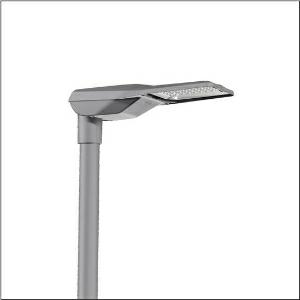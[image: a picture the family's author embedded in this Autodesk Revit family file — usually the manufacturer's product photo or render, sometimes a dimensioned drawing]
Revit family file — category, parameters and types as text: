
# Revit family: streetlight_sl_21_iq_mini___stw1_0a_5xe2e31g08jb_fb58
name_source: partatom
category: Lighting Fixtures
units: mm (PartAtom-declared; Revit-internal decimal feet)

## family parameters
Cut with Voids When Loaded = No
Host = Face
Light Source = No
Part Type = Normal
Room Calculation Point = No
Round Connector Dimension = Use Diameter
Shared = No

## types (1)
- --- (1 x LED, 10820 lm, 71.6 W, 3000K)
    Apparent Load = 72 VA
    CIE Flux Codes = 39 75 98 100 100
    Color Rendering = 70
    Color Temperature = 3000K
    Default Elevation = 1800 mm
    Description = Streetlight SL 21 iQ mini, mast luminaire, primary light control with lens, of PMMA, primary optical cover: cover, of toughened safety glass, transparent, light distribution: STW1.0a, light emission: direct distribution, primary light characteristic: asymmetric, installation type: post-top, side-entry, LED, High Power LED, rated luminous flux: 10.820lm, luminous efficacy: 151lm/W, light colour: 730, colour temperature: 3000K, control gear: iQ Street-Remote, control: Street-Remote, Auto-Match, Temp-Guard, Lumen-Switch, Night-Set, Smart-Wire, Light-Fading, Desk-Remote (wireless, voltage-free reading and setting of iQ features in the workshop via application-optimized NFC function/RFID function), optimised constant luminous flux control (CLO 2.0), pre-setting: linear dimming characteristic, mains connection: 220..240V, AC, 50/60Hz, start of lifetime: 72W, end of service life: 75W, reduction: 33W, luminaire housing, of diecast aluminium, powder-coated, Siteco® metallic grey (DB 702S), corrosivity category C5 mid according to DIN EN ISO 12944, please order mast flange separately, inclination adjustable: 0°, 5°, 10°, 15°, sealing non-destructively replaceable, multi-level sealing system, length: 628mm, width: 235mm, height: 110mm, mast flange for spigot size: 42mm (side-entry): 5XC10008XM4, 60/48mm (side-entry/post-top): 5XC10108XM2, 76/60mm (side-entry/post-top): 5XC10108XM1, mounting height: 4..8m, protection rating (complete): IP66, insulation class (complete): insulation class II (safety insulation), certification: CE, ENEC, ENEC+, VDE, impact resistance: IK10, permissible operating ambient temperature for outdoor applications: -40..+50°C, standard-compliant lighting for roads and squares, packaging unit: 1 piece

Light Distribution: STW1.0a
    Height = 110 mm
    Lamp = 1 x LED
    Lamp Light Flux = 10820 lm
    Lamp Power = 71.6 W
    Lamp count = 1
    Length = 625 mm
    Luminous efficacy = 151 lm/W
    Manufacturer = Siteco
    ModVariant = No
    Model = 5XE2E31G08JB
    Number of Poles = 1
    OnlyDefault = Yes
    Power Factor = 1
    Product Name = Streetlight SL 21 iQ mini | STW1.0a
    Product group = mast luminaire | pylon top
    ProductGroupID = 6100
    Protection Class = Protection class II
    Protection Degree = IP 66
    RLX_Detail_Level = 1
    RLX_Emergency_Light_Flux = 0 lm
    RLX_Emergency_Type = 0
    RLX_Emergency_Type_DB = No
    RlxData = <blob elided: 26405 chars, md5=772471f9>
    Socket = socket
    Standby Power = 0 W
    System Light Flux = 10820 lm
    System Power = 72 W
    Type Comments = factory setting: luminous flux: 100 % | dim-lin: 254 | 746 mA
    Type Image = l_1003519.jpg
    URL = http://relux.com
    VarID = @adj_191661
    Voltage = 0 V
    Weight = 0.00 kg
    Width = 234 mm

## geometry (parser evidence)
native form markers: Blend x4, Sweep x10
no freeform markers — native parametric forms only
